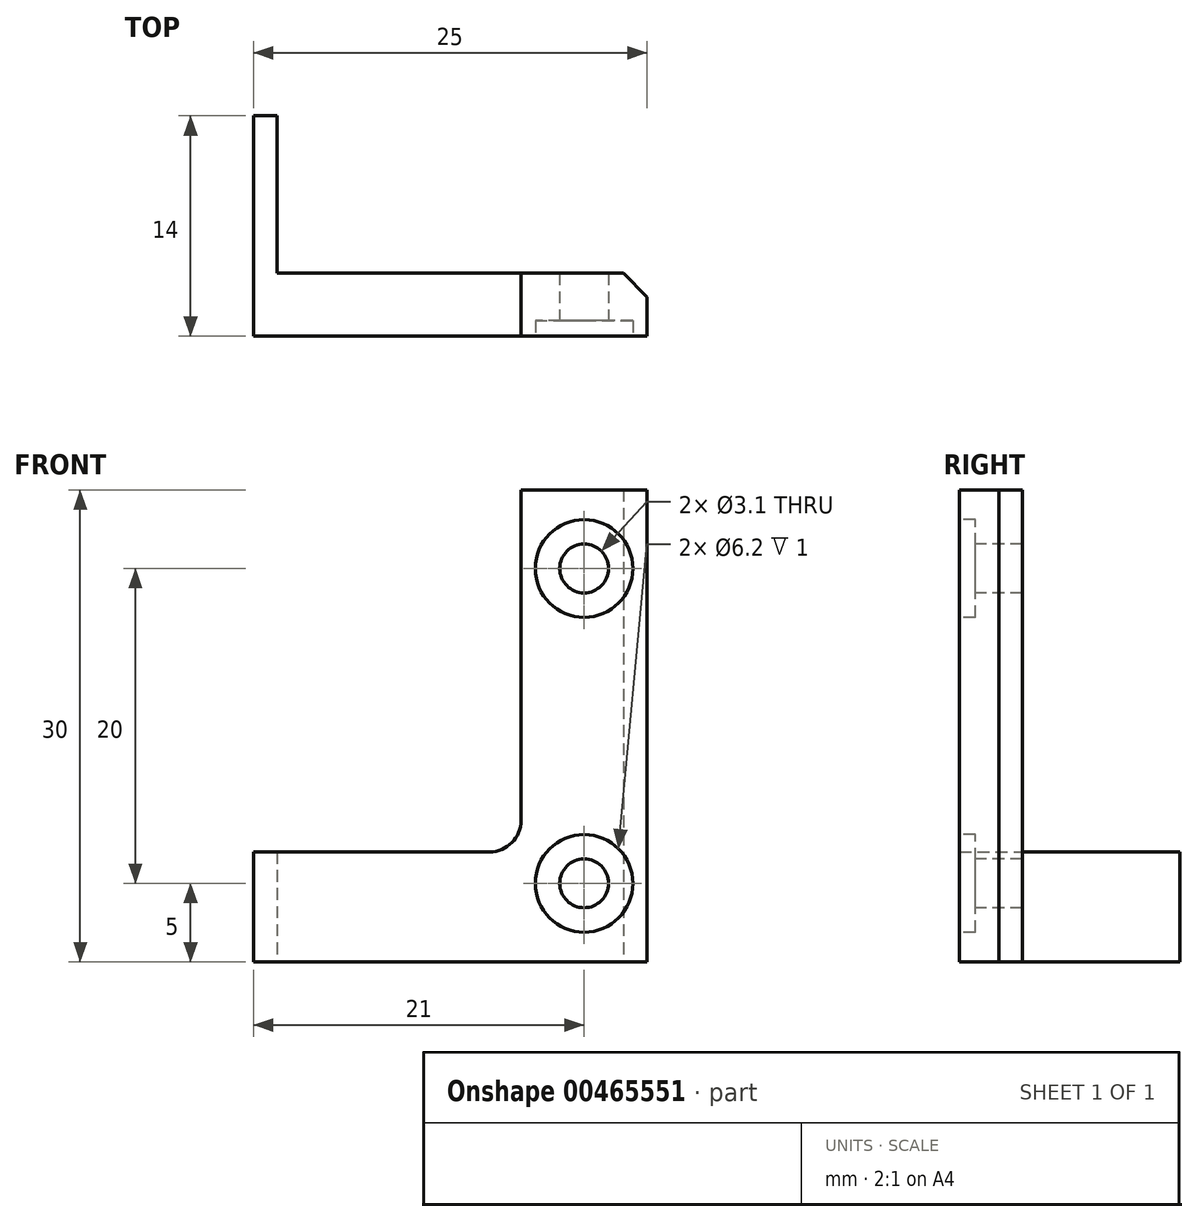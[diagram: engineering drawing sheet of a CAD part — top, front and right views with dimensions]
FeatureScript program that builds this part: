
annotation { "Feature Type Name" : "Feature", "Feature Type Description" : "" }
export const myFeature = defineFeature(function(context is Context, id is Id, definition is map)
    precondition{}
    {
        {
            var Q0;
            Q0=qCreatedBy(makeId("Front.planeOp"),FACE);
            var sketch = newSketch(context, id + "F0", { "sketchPlane" : qUnion([Q0])});
            skLineSegment(sketch, "E0", {"start": v(8, 0) * mm, "end": v(8, 30) * mm});
            skLineSegment(sketch, "E1", {"start": v(8, 30) * mm, "end": v(0, 30) * mm});
            skLineSegment(sketch, "E2", {"start": v(0, 30) * mm, "end": v(0, 7) * mm});
            skLineSegment(sketch, "E3", {"start": v(0, 7) * mm, "end": v(-17, 7) * mm});
            skLineSegment(sketch, "E4", {"start": v(-17, 7) * mm, "end": v(-17, 0) * mm});
            skLineSegment(sketch, "E5", {"start": v(-17, 0) * mm, "end": v(8, 0) * mm});
            skSolve(sketch);
        }
        {
            var Q0;
            Q0=makeQuery(id+"F0.imprint","IMPRINT",FACE,{"disambiguationData":[TD([[makeQuery(id+"F0.imprint","IMPRINT",EDGE,{"derivedFrom":sQuery(id+"F0.wireOp",EDGE,"E0")}),1.0]])]});
            extrude(context, id + "F1", {"entities" : qUnion([Q0]), "depth" : 4 * mm});
        }
        {
            var Q0;
            Q0=makeQuery(id+"F1.opExtrude","CAP_FACE",FACE,{"disambiguationData":[OSD([sQuery(id+"F0.wireOp",EDGE,"E0"),sQuery(id+"F0.wireOp",EDGE,"E1"),sQuery(id+"F0.wireOp",EDGE,"E2"),sQuery(id+"F0.wireOp",EDGE,"E3"),sQuery(id+"F0.wireOp",EDGE,"E4"),sQuery(id+"F0.wireOp",EDGE,"E5")])],"isStart":false});
            var sketch = newSketch(context, id + "F2", { "sketchPlane" : qUnion([Q0])});
            skPoint(sketch, "E6", {"position": v(4, 25) * mm});
            skPoint(sketch, "E7", {"position": v(4, 5) * mm});
            skSolve(sketch);
        }
        {
            var Q0;
            Q0=sQuery(id+"F2.wireOp",VERTEX,"E6");
            var Q1;
            Q1=sQuery(id+"F2.wireOp",VERTEX,"E7");
            var Q2;
            Q2=makeQuery(id+"F1.opExtrude","SWEPT_BODY",BODY,{"disambiguationData":[OSD([sQuery(id+"F0.wireOp",EDGE,"E0"),sQuery(id+"F0.wireOp",EDGE,"E1"),sQuery(id+"F0.wireOp",EDGE,"E2"),sQuery(id+"F0.wireOp",EDGE,"E3"),sQuery(id+"F0.wireOp",EDGE,"E4"),sQuery(id+"F0.wireOp",EDGE,"E5")])]});
            hole(context, id + "F3", {"style" : HoleStyle.C_BORE, "endStyle" : HoleEndStyle.THROUGH, "holeDiameter" : 3.1 * mm, "cBoreDiameter" : 6.2 * mm, "cBoreDepth" : 1 * mm, "tappedDepth" : 12 * mm, "tapClearance" : 3, "locations" : qUnion([Q0, Q1]), "scope" : qUnion([Q2])});
        }
        {
            var Q0;
            Q0=qCreatedBy(makeId("Front.planeOp"),FACE);
            var sketch = newSketch(context, id + "F4", { "sketchPlane" : qUnion([Q0])});
            skLineSegment(sketch, "E8.bottom", {"start": v(-15.5, 7) * mm, "end": v(-17, 7) * mm});
            skLineSegment(sketch, "E8.top", {"start": v(-15.5, 0) * mm, "end": v(-17, 0) * mm});
            skLineSegment(sketch, "E8.left", {"start": v(-15.5, 7) * mm, "end": v(-15.5, 0) * mm});
            skLineSegment(sketch, "E8.right", {"start": v(-17, 7) * mm, "end": v(-17, 0) * mm});
            skSolve(sketch);
        }
        {
            var Q0;
            Q0 = qSketchRegion(id + "F4", true);
            extrude(context, id + "F5", {"entities" : qUnion([Q0]), "operationType" : NewBodyOperationType.ADD, "oppositeDirection" : true, "depth" : 10 * mm});
        }
        {
            var Q0;
            Q0=makeQuery(id+"F1.opExtrude","CAP_EDGE",EDGE,{"disambiguationData":[OSD([sQuery(id+"F0.wireOp",EDGE,"E0")])],"isStart":true});
            chamfer(context, id + "F6", {"entities" : qUnion([Q0]), "width" : 1.5 * mm, "tangentPropagation" : true});
        }
        {
            var Q0;
            Q0=makeQuery(id+"F5.opExtrude","CAP_EDGE",EDGE,{"disambiguationData":[OSD([sQuery(id+"F4.wireOp",EDGE,"E8.left")])],"isStart":true});
            var Q1;
            Q1=makeQuery(id+"F1.opExtrude","SWEPT_EDGE",EDGE,{"disambiguationData":[OSD([sQuery(id+"F0.wireOp",EDGE,"E2"),sQuery(id+"F0.wireOp",EDGE,"E3")])]});
            fillet(context, id + "F7", {"entities" : qUnion([Q0, Q1]), "radius" : 2 * mm, "tangentPropagation" : true, "allowEdgeOverflow" : false});
        }
    });
